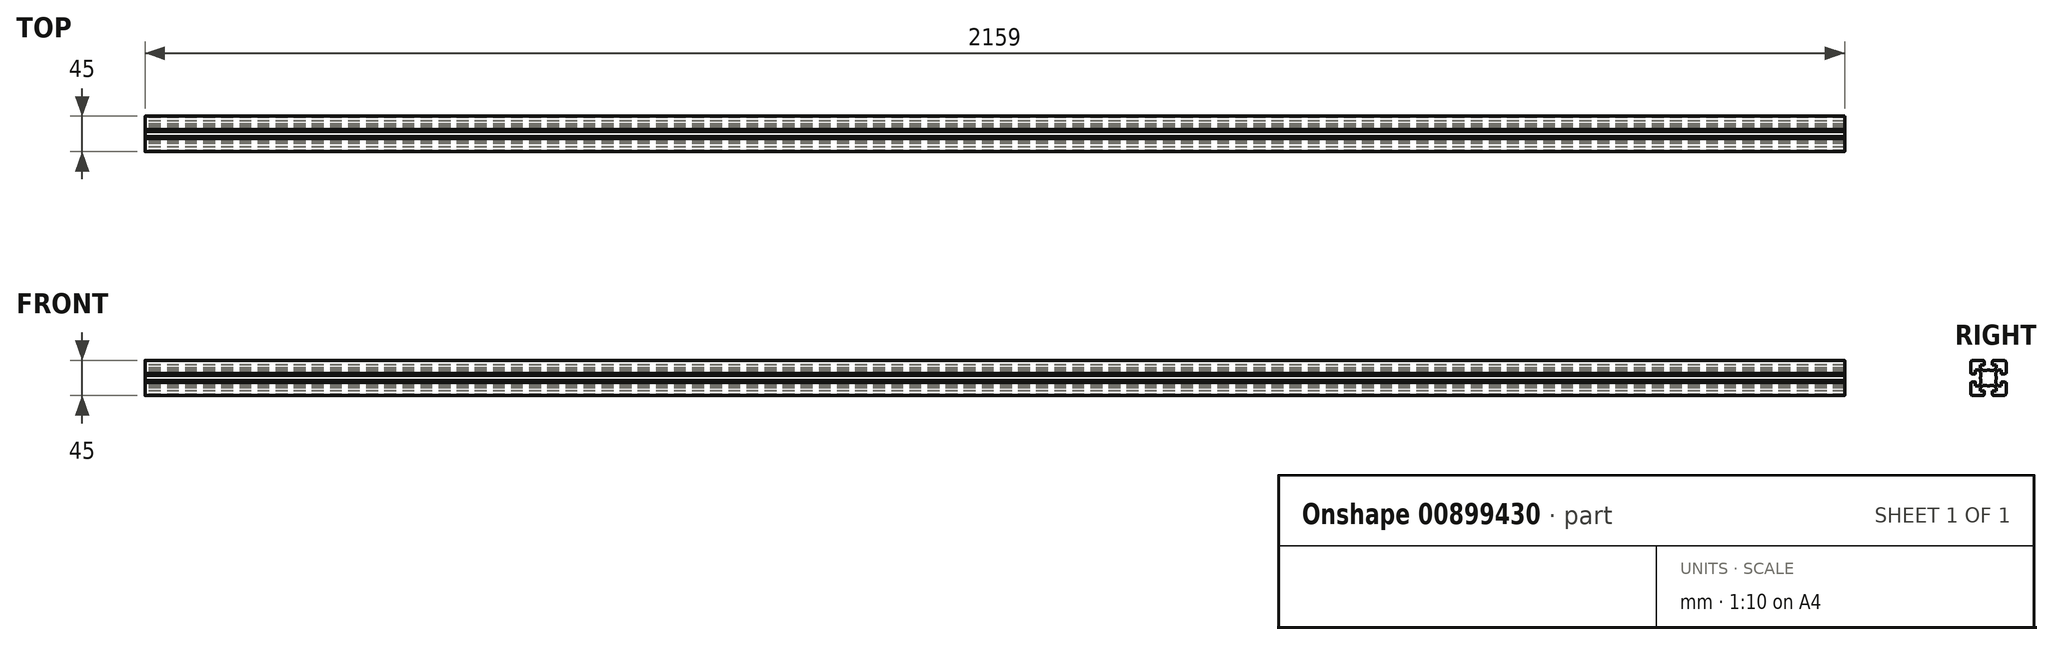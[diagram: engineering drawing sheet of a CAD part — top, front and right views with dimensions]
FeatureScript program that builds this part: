
annotation { "Feature Type Name" : "Feature", "Feature Type Description" : "" }
export const myFeature = defineFeature(function(context is Context, id is Id, definition is map)
    precondition{}
    {
        {
            var Q0;
            Q0=qCreatedBy(makeId("Right.planeOp"),FACE);
            var sketch = newSketch(context, id + "F0", { "sketchPlane" : qUnion([Q0])});
            skLineSegment(sketch, "E0", {"start": v(-20.09, -10.29) * mm, "end": v(-21.29, -10.29) * mm});
            skArc(sketch, "E1", {"start": v(-21.29, -10.29) * mm, "mid": v(-21.5, -10.38) * mm, "end": v(-21.59, -10.59) * mm});
            skLineSegment(sketch, "E2", {"start": v(-21.59, -10.59) * mm, "end": v(-21.59, -23.99) * mm});
            skArc(sketch, "E3", {"start": v(-21.59, -23.99) * mm, "mid": v(-20.7, -26.11) * mm, "end": v(-18.59, -26.99) * mm});
            skLineSegment(sketch, "E4", {"start": v(-18.59, -26.99) * mm, "end": v(-5.19, -26.99) * mm});
            skArc(sketch, "E5", {"start": v(-5.19, -26.99) * mm, "mid": v(-4.98, -26.9) * mm, "end": v(-4.89, -26.69) * mm});
            skLineSegment(sketch, "E6", {"start": v(-4.89, -26.69) * mm, "end": v(-4.89, -25.49) * mm});
            skLineSegment(sketch, "E7", {"start": v(-4.89, -25.49) * mm, "end": v(-4.39, -25.49) * mm});
            skArc(sketch, "E8", {"start": v(-4.39, -25.49) * mm, "mid": v(-4.18, -25.4) * mm, "end": v(-4.09, -25.19) * mm});
            skLineSegment(sketch, "E9", {"start": v(-4.09, -25.19) * mm, "end": v(-4.09, -21.29) * mm});
            skArc(sketch, "E10", {"start": v(-4.09, -21.29) * mm, "mid": v(-4.18, -21.08) * mm, "end": v(-4.39, -20.99) * mm});
            skLineSegment(sketch, "E11", {"start": v(-4.39, -20.99) * mm, "end": v(-9.14, -20.99) * mm});
            skLineSegment(sketch, "E12", {"start": v(-9.14, -20.99) * mm, "end": v(-9.14, -16.88) * mm});
            skLineSegment(sketch, "E13", {"start": v(-9.14, -16.88) * mm, "end": v(-6.25, -13.99) * mm});
            skLineSegment(sketch, "E14", {"start": v(-6.25, -13.99) * mm, "end": v(-2.21, -13.99) * mm});
            skArc(sketch, "E15", {"start": v(-2.21, -13.99) * mm, "mid": v(0.91, -14.49) * mm, "end": v(4.03, -13.99) * mm});
            skLineSegment(sketch, "E16", {"start": v(-20.09, -10.29) * mm, "end": v(-20.09, -9.79) * mm});
            skArc(sketch, "E17", {"start": v(-20.09, -9.79) * mm, "mid": v(-20, -9.58) * mm, "end": v(-19.79, -9.49) * mm});
            skLineSegment(sketch, "E18", {"start": v(-19.79, -9.49) * mm, "end": v(-15.89, -9.49) * mm});
            skArc(sketch, "E19", {"start": v(-15.89, -9.49) * mm, "mid": v(-15.68, -9.58) * mm, "end": v(-15.59, -9.79) * mm});
            skLineSegment(sketch, "E20", {"start": v(-15.59, -9.79) * mm, "end": v(-15.59, -14.54) * mm});
            skLineSegment(sketch, "E21", {"start": v(-15.59, -14.54) * mm, "end": v(-11.48, -14.54) * mm});
            skLineSegment(sketch, "E22", {"start": v(-11.48, -14.54) * mm, "end": v(-8.59, -11.65) * mm});
            skLineSegment(sketch, "E23", {"start": v(-8.59, -11.65) * mm, "end": v(-8.59, -7.61) * mm});
            skLineSegment(sketch, "E24", {"start": v(29.82, -4.49) * mm, "end": v(-31.05, -4.49) * mm});
            skLineSegment(sketch, "E25.MirrorCS", {"start": v(6.71, -25.49) * mm, "end": v(6.21, -25.49) * mm});
            skArc(sketch, "E26.MirrorCS", {"start": v(7.01, -26.99) * mm, "mid": v(6.8, -26.9) * mm, "end": v(6.71, -26.69) * mm});
            skLineSegment(sketch, "E27.MirrorCS", {"start": v(10.41, -11.65) * mm, "end": v(10.41, -7.61) * mm});
            skArc(sketch, "E28.MirrorCS", {"start": v(6.21, -25.49) * mm, "mid": v(6, -25.4) * mm, "end": v(5.91, -25.19) * mm});
            skLineSegment(sketch, "E29.MirrorCS", {"start": v(6.71, -26.69) * mm, "end": v(6.71, -25.49) * mm});
            skArc(sketch, "E30.MirrorCS", {"start": v(5.91, -21.29) * mm, "mid": v(6, -21.08) * mm, "end": v(6.21, -20.99) * mm});
            skLineSegment(sketch, "E31.MirrorCS", {"start": v(10.96, -16.88) * mm, "end": v(8.07, -13.99) * mm});
            skLineSegment(sketch, "E32.MirrorCS", {"start": v(13.3, -14.54) * mm, "end": v(10.41, -11.65) * mm});
            skLineSegment(sketch, "E33.MirrorCS", {"start": v(17.41, -14.54) * mm, "end": v(13.3, -14.54) * mm});
            skLineSegment(sketch, "E34.MirrorCS", {"start": v(17.41, -9.79) * mm, "end": v(17.41, -14.54) * mm});
            skLineSegment(sketch, "E35.MirrorCS", {"start": v(6.21, -20.99) * mm, "end": v(10.96, -20.99) * mm});
            skLineSegment(sketch, "E36.MirrorCS", {"start": v(8.07, -13.99) * mm, "end": v(4.03, -13.99) * mm});
            skArc(sketch, "E37.MirrorCS", {"start": v(4.03, -13.99) * mm, "mid": v(0.91, -14.49) * mm, "end": v(-2.21, -13.99) * mm});
            skLineSegment(sketch, "E38.MirrorCS", {"start": v(10.96, -20.99) * mm, "end": v(10.96, -16.88) * mm});
            skLineSegment(sketch, "E39.MirrorCS", {"start": v(5.91, -25.19) * mm, "end": v(5.91, -21.29) * mm});
            skArc(sketch, "E40.MirrorCS", {"start": v(23.41, -23.99) * mm, "mid": v(22.53, -26.11) * mm, "end": v(20.41, -26.99) * mm});
            skLineSegment(sketch, "E41.MirrorCS", {"start": v(20.41, -26.99) * mm, "end": v(7.01, -26.99) * mm});
            skLineSegment(sketch, "E42.MirrorCS", {"start": v(23.41, -10.59) * mm, "end": v(23.41, -23.99) * mm});
            skArc(sketch, "E43.MirrorCS", {"start": v(17.71, -9.49) * mm, "mid": v(17.5, -9.58) * mm, "end": v(17.41, -9.79) * mm});
            skArc(sketch, "E44.MirrorCS", {"start": v(23.11, -10.29) * mm, "mid": v(23.32, -10.38) * mm, "end": v(23.41, -10.59) * mm});
            skLineSegment(sketch, "E45.MirrorCS", {"start": v(21.91, -10.29) * mm, "end": v(21.91, -9.79) * mm});
            skLineSegment(sketch, "E46.MirrorCS", {"start": v(21.91, -10.29) * mm, "end": v(23.11, -10.29) * mm});
            skArc(sketch, "E47.MirrorCS", {"start": v(21.91, -9.79) * mm, "mid": v(21.82, -9.58) * mm, "end": v(21.61, -9.49) * mm});
            skLineSegment(sketch, "E48.MirrorCS", {"start": v(21.61, -9.49) * mm, "end": v(17.71, -9.49) * mm});
            skLineSegment(sketch, "E49.MirrorCS", {"start": v(6.71, 16.51) * mm, "end": v(6.21, 16.51) * mm});
            skArc(sketch, "E50.MirrorCS", {"start": v(-4.39, 16.51) * mm, "mid": v(-4.18, 16.42) * mm, "end": v(-4.09, 16.21) * mm});
            skLineSegment(sketch, "E51.MirrorCS", {"start": v(-4.89, 16.51) * mm, "end": v(-4.39, 16.51) * mm});
            skArc(sketch, "E52.MirrorCS", {"start": v(5.91, 12.31) * mm, "mid": v(6, 12.1) * mm, "end": v(6.21, 12.01) * mm});
            skLineSegment(sketch, "E53.MirrorCS", {"start": v(6.71, 17.71) * mm, "end": v(6.71, 16.51) * mm});
            skLineSegment(sketch, "E54.MirrorCS", {"start": v(-4.89, 17.71) * mm, "end": v(-4.89, 16.51) * mm});
            skArc(sketch, "E55.MirrorCS", {"start": v(-5.19, 18.01) * mm, "mid": v(-4.98, 17.92) * mm, "end": v(-4.89, 17.71) * mm});
            skArc(sketch, "E56.MirrorCS", {"start": v(-4.09, 12.31) * mm, "mid": v(-4.18, 12.1) * mm, "end": v(-4.39, 12.01) * mm});
            skArc(sketch, "E57.MirrorCS", {"start": v(7.01, 18.01) * mm, "mid": v(6.8, 17.92) * mm, "end": v(6.71, 17.71) * mm});
            skArc(sketch, "E58.MirrorCS", {"start": v(6.21, 16.51) * mm, "mid": v(6, 16.42) * mm, "end": v(5.91, 16.21) * mm});
            skArc(sketch, "E59.MirrorCS", {"start": v(23.11, 1.31) * mm, "mid": v(23.32, 1.4) * mm, "end": v(23.41, 1.61) * mm});
            skLineSegment(sketch, "E60.MirrorCS", {"start": v(21.91, 1.31) * mm, "end": v(21.91, 0.81) * mm});
            skArc(sketch, "E61.MirrorCS", {"start": v(-15.89, 0.51) * mm, "mid": v(-15.68, 0.6) * mm, "end": v(-15.59, 0.81) * mm});
            skArc(sketch, "E62.MirrorCS", {"start": v(-21.29, 1.31) * mm, "mid": v(-21.5, 1.4) * mm, "end": v(-21.59, 1.61) * mm});
            skArc(sketch, "E63.MirrorCS", {"start": v(17.71, 0.51) * mm, "mid": v(17.5, 0.6) * mm, "end": v(17.41, 0.81) * mm});
            skArc(sketch, "E64.MirrorCS", {"start": v(21.91, 0.81) * mm, "mid": v(21.82, 0.6) * mm, "end": v(21.61, 0.51) * mm});
            skLineSegment(sketch, "E65.MirrorCS", {"start": v(21.91, 1.31) * mm, "end": v(23.11, 1.31) * mm});
            skArc(sketch, "E66.MirrorCS", {"start": v(14.31, 5.31) * mm, "mid": v(14.1, 5.4) * mm, "end": v(14.01, 5.61) * mm});
            skArc(sketch, "E67.MirrorCS", {"start": v(-20.09, 0.81) * mm, "mid": v(-20, 0.6) * mm, "end": v(-19.79, 0.51) * mm});
            skLineSegment(sketch, "E68.MirrorCS", {"start": v(-20.09, 1.31) * mm, "end": v(-21.29, 1.31) * mm});
            skLineSegment(sketch, "E69.MirrorCS", {"start": v(-20.09, 1.31) * mm, "end": v(-20.09, 0.81) * mm});
            skLineSegment(sketch, "E70.MirrorCS", {"start": v(8.07, 5.01) * mm, "end": v(4.03, 5.01) * mm});
            skLineSegment(sketch, "E71.MirrorCS", {"start": v(-4.09, 16.21) * mm, "end": v(-4.09, 12.31) * mm});
            skLineSegment(sketch, "E72.MirrorCS", {"start": v(-9.14, 12.01) * mm, "end": v(-9.14, 7.9) * mm});
            skLineSegment(sketch, "E73.MirrorCS", {"start": v(-15.59, 5.56) * mm, "end": v(-11.48, 5.56) * mm});
            skLineSegment(sketch, "E74.MirrorCS", {"start": v(-4.39, 12.01) * mm, "end": v(-9.14, 12.01) * mm});
            skLineSegment(sketch, "E75.MirrorCS", {"start": v(-9.14, 7.9) * mm, "end": v(-6.25, 5.01) * mm});
            skLineSegment(sketch, "E76.MirrorCS", {"start": v(10.96, 12.01) * mm, "end": v(10.96, 7.9) * mm});
            skArc(sketch, "E77.MirrorCS", {"start": v(-21.59, 15.01) * mm, "mid": v(-20.7, 17.13) * mm, "end": v(-18.59, 18.01) * mm});
            skLineSegment(sketch, "E78.MirrorCS", {"start": v(23.41, 1.61) * mm, "end": v(23.41, 15.01) * mm});
            skLineSegment(sketch, "E79.MirrorCS", {"start": v(13.3, 5.56) * mm, "end": v(10.41, 2.67) * mm});
            skLineSegment(sketch, "E80.MirrorCS", {"start": v(-8.59, 2.67) * mm, "end": v(-8.59, -1.37) * mm});
            skLineSegment(sketch, "E81.MirrorCS", {"start": v(-15.59, 0.81) * mm, "end": v(-15.59, 5.56) * mm});
            skLineSegment(sketch, "E82.MirrorCS", {"start": v(10.41, 2.67) * mm, "end": v(10.41, -1.37) * mm});
            skLineSegment(sketch, "E83.MirrorCS", {"start": v(-18.59, 18.01) * mm, "end": v(-5.19, 18.01) * mm});
            skLineSegment(sketch, "E84.MirrorCS", {"start": v(10.96, 7.9) * mm, "end": v(8.07, 5.01) * mm});
            skLineSegment(sketch, "E85.MirrorCS", {"start": v(17.41, 5.56) * mm, "end": v(13.3, 5.56) * mm});
            skArc(sketch, "E86.MirrorCS", {"start": v(23.41, 15.01) * mm, "mid": v(22.53, 17.13) * mm, "end": v(20.41, 18.01) * mm});
            skLineSegment(sketch, "E87.MirrorCS", {"start": v(5.91, 16.21) * mm, "end": v(5.91, 12.31) * mm});
            skLineSegment(sketch, "E88.MirrorCS", {"start": v(17.41, 0.81) * mm, "end": v(17.41, 5.56) * mm});
            skLineSegment(sketch, "E89.MirrorCS", {"start": v(-11.48, 5.56) * mm, "end": v(-8.59, 2.67) * mm});
            skLineSegment(sketch, "E90.MirrorCS", {"start": v(-6.25, 5.01) * mm, "end": v(-2.21, 5.01) * mm});
            skLineSegment(sketch, "E91.MirrorCS", {"start": v(-21.59, 1.61) * mm, "end": v(-21.59, 15.01) * mm});
            skArc(sketch, "E92.MirrorCS", {"start": v(4.03, 5.01) * mm, "mid": v(0.91, 5.51) * mm, "end": v(-2.21, 5.01) * mm});
            skLineSegment(sketch, "E93.MirrorCS", {"start": v(6.21, 12.01) * mm, "end": v(10.96, 12.01) * mm});
            skArc(sketch, "E94.MirrorCS", {"start": v(-2.21, 5.01) * mm, "mid": v(0.91, 5.51) * mm, "end": v(4.03, 5.01) * mm});
            skLineSegment(sketch, "E95.MirrorCS", {"start": v(20.41, 18.01) * mm, "end": v(7.01, 18.01) * mm});
            skLineSegment(sketch, "E96.MirrorCS", {"start": v(-19.79, 0.51) * mm, "end": v(-15.89, 0.51) * mm});
            skLineSegment(sketch, "E97.MirrorCS", {"start": v(21.61, 0.51) * mm, "end": v(17.71, 0.51) * mm});
            skLineSegment(sketch, "E98.MirrorCS", {"start": v(0.91, -27.65) * mm, "end": v(0.91, 19.82) * mm});
            skArc(sketch, "E99", {"start": v(-8.59, -1.37) * mm, "mid": v(-9.09, -4.49) * mm, "end": v(-8.59, -7.61) * mm});
            skArc(sketch, "E100", {"start": v(10.41, -7.61) * mm, "mid": v(10.91, -4.49) * mm, "end": v(10.41, -1.37) * mm});
            skSolve(sketch);
        }
        {
            var Q0;
            Q0=qSketchRegion(id+"F0",true);
            extrude(context, id + "F1", {"entities" : qUnion([Q0]), "depth" : 2159 * mm, "offsetDistance" : 25.4 * mm});
        }
    });
